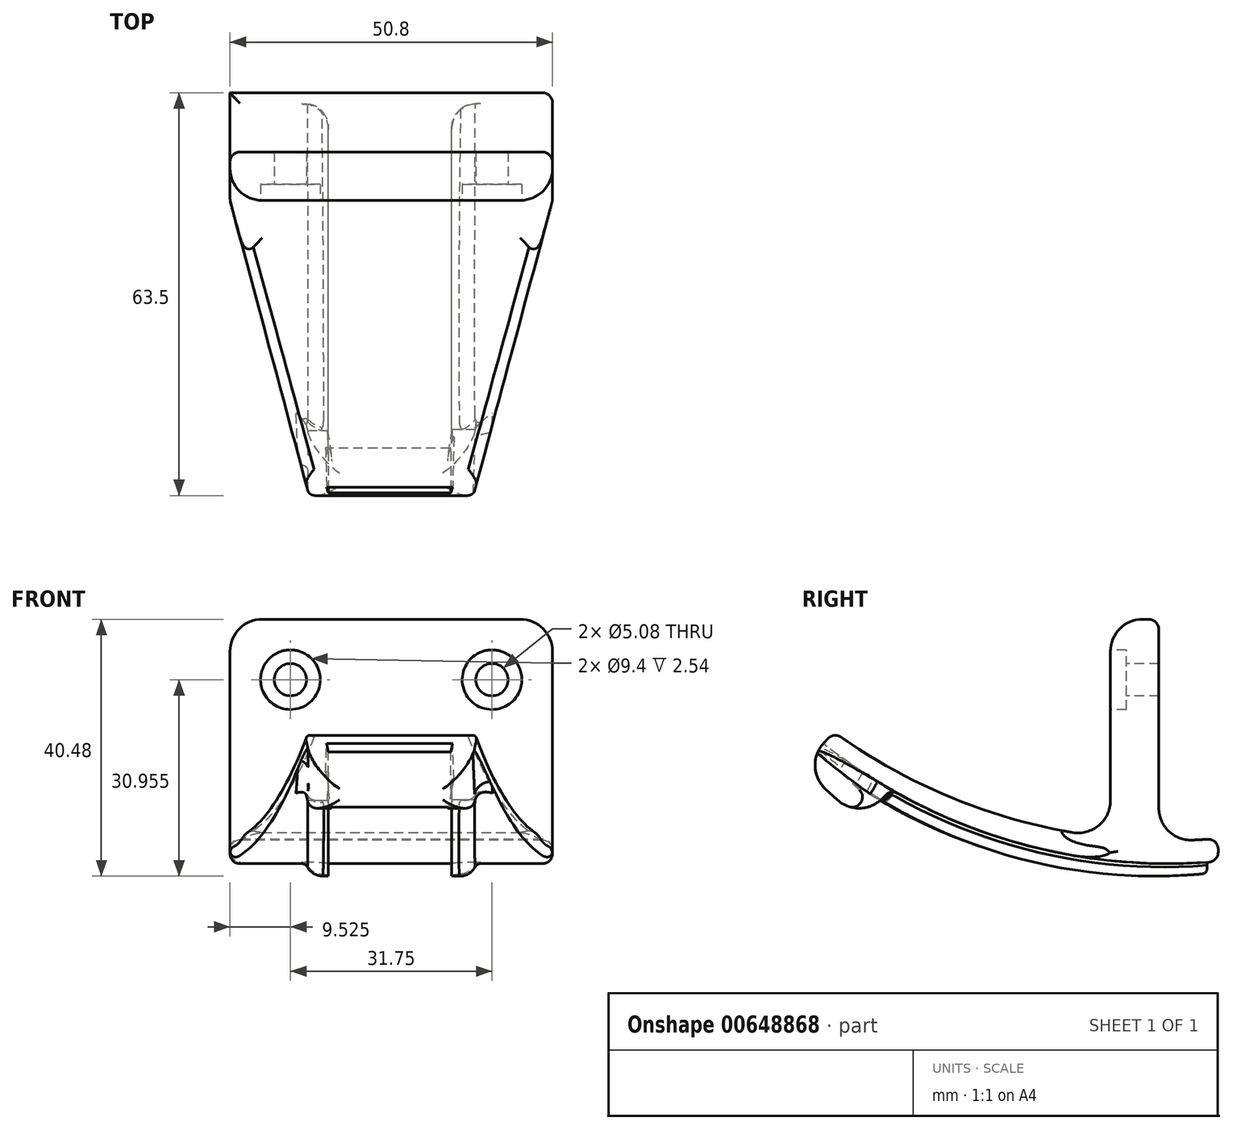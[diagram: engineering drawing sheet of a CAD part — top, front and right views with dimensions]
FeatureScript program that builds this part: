
annotation { "Feature Type Name" : "Feature", "Feature Type Description" : "" }
export const myFeature = defineFeature(function(context is Context, id is Id, definition is map)
    precondition{}
    {
        {
            var Q0;
            Q0=qCreatedBy(makeId("Front.planeOp"),FACE);
            var sketch = newSketch(context, id + "F0", { "sketchPlane" : qUnion([Q0])});
            skLineSegment(sketch, "E0.bottom", {"start": v(25.4, -17.78) * mm, "end": v(-25.4, -17.78) * mm});
            skLineSegment(sketch, "E0.top", {"start": v(25.4, 17.78) * mm, "end": v(-25.4, 17.78) * mm});
            skLineSegment(sketch, "E0.left", {"start": v(25.4, -17.78) * mm, "end": v(25.4, 17.78) * mm});
            skLineSegment(sketch, "E0.right", {"start": v(-25.4, -17.78) * mm, "end": v(-25.4, 17.78) * mm});
            skPoint(sketch, "E0.middle", {"position": v(0, 0) * mm});
            skPoint(sketch, "E1", {"position": v(-15.88, 8.26) * mm});
            skPoint(sketch, "E2", {"position": v(15.87, 8.26) * mm});
            skSolve(sketch);
        }
        {
            var Q0;
            Q0=makeQuery(id+"F0.imprint","IMPRINT",FACE,{"disambiguationData":[TD([[makeQuery(id+"F0.imprint","IMPRINT",EDGE,{"derivedFrom":sQuery(id+"F0.wireOp",EDGE,"E0.bottom")}),-1.0]])]});
            extrude(context, id + "F1", {"entities" : qUnion([Q0]), "oppositeDirection" : true, "depth" : 7.62 * mm, "offsetDistance" : 25.4 * mm});
        }
        {
            var Q0;
            Q0=qCreatedBy(makeId("Front.planeOp"),FACE);
            var sketch = newSketch(context, id + "F2", { "sketchPlane" : qUnion([Q0])});
            skPoint(sketch, "E3", {"position": v(-15.88, 8.26) * mm});
            skPoint(sketch, "E4", {"position": v(15.87, 8.26) * mm});
            skSolve(sketch);
        }
        {
            var Q0;
            Q0=sQuery(id+"F2.wireOp",VERTEX,"E3");
            var Q1;
            Q1=sQuery(id+"F2.wireOp",VERTEX,"E4");
            var Q2;
            Q2=makeQuery(id+"F1.opExtrude","SWEPT_BODY",BODY,{"disambiguationData":[OSD([sQuery(id+"F0.wireOp",EDGE,"E0.bottom"),sQuery(id+"F0.wireOp",EDGE,"E0.top"),sQuery(id+"F0.wireOp",EDGE,"E0.left"),sQuery(id+"F0.wireOp",EDGE,"E0.right")])]});
            hole(context, id + "F3", {"style" : HoleStyle.C_BORE, "endStyle" : HoleEndStyle.BLIND, "holeDiameter" : 5.08 * mm, "cBoreDiameter" : 9.4 * mm, "cBoreDepth" : 2.54 * mm, "majorDiameter" : 6.35 * mm, "holeDepth" : 7.62 * mm, "isTappedThrough" : true, "tappedDepth" : 12.7 * mm, "tapClearance" : 3, "locations" : qUnion([Q0, Q1]), "scope" : qUnion([Q2])});
        }
        {
            var Q0;
            Q0=qCreatedBy(makeId("Right.planeOp"),FACE);
            cPlane(context, id + "F4", {"entities" : qUnion([Q0]), "cplaneType" : CPlaneType.OFFSET, "offset" : 25.4 * mm, "oppositeDirection" : true, "width" : 152.4 * mm, "height" : 152.4 * mm});
        }
        {
            var Q0;
            Q0=qCreatedBy(id+"F4.planeOp",FACE);
            var sketch = newSketch(context, id + "F5", { "sketchPlane" : qUnion([Q0])});
            skArc(sketch, "E5", {"start": v(-43.55, 0) * mm, "mid": v(-14.8, -13.85) * mm, "end": v(16.98, -16.76) * mm});
            skArc(sketch, "E6", {"start": v(-45.22, -1.81) * mm, "mid": v(-15.9, -17.1) * mm, "end": v(16.98, -20.38) * mm});
            skLineSegment(sketch, "E7", {"start": v(-45.22, -1.81) * mm, "end": v(-43.55, 0) * mm});
            skLineSegment(sketch, "E8", {"start": v(16.98, -20.38) * mm, "end": v(16.98, -16.76) * mm});
            skSolve(sketch);
        }
        {
            var Q0;
            Q0=makeQuery(id+"F5.imprint","IMPRINT",FACE,{"disambiguationData":[TD([[makeQuery(id+"F5.imprint","IMPRINT",EDGE,{"derivedFrom":sQuery(id+"F5.wireOp",EDGE,"E5")}),-1.0]])]});
            extrude(context, id + "F6", {"entities" : qUnion([Q0]), "operationType" : NewBodyOperationType.ADD, "depth" : 50.8 * mm, "offsetDistance" : 25.4 * mm});
        }
        {
            var Q0;
            Q0=qCreatedBy(makeId("Right.planeOp"),FACE);
            var Q1;
            Q1=sQuery(id+"F0.wireOp",EDGE,"E0.left");
            cPlane(context, id + "F7", {"entities" : qUnion([Q0, Q1]), "cplaneType" : CPlaneType.LINE_ANGLE, "offset" : 25.4 * mm, "angle" : 15 * degree, "oppositeDirection" : true, "width" : 152.4 * mm, "height" : 152.4 * mm});
        }
        {
            var Q0;
            Q0=qCreatedBy(makeId("Right.planeOp"),FACE);
            var Q1;
            Q1=sQuery(id+"F0.wireOp",EDGE,"E0.right");
            cPlane(context, id + "F8", {"entities" : qUnion([Q0, Q1]), "cplaneType" : CPlaneType.LINE_ANGLE, "offset" : 25.4 * mm, "angle" : 15 * degree, "width" : 152.4 * mm, "height" : 152.4 * mm});
        }
        {
            var Q0;
            Q0=qCreatedBy(id+"F7.planeOp",FACE);
            var sketch = newSketch(context, id + "F9", { "sketchPlane" : qUnion([Q0])});
            skLineSegment(sketch, "E9.bottom", {"start": v(-11.2, 0) * mm, "end": v(43.96, 0) * mm});
            skLineSegment(sketch, "E9.top", {"start": v(-11.2, -22.32) * mm, "end": v(43.96, -22.32) * mm});
            skLineSegment(sketch, "E9.left", {"start": v(-11.2, 0) * mm, "end": v(-11.2, -22.32) * mm});
            skLineSegment(sketch, "E9.right", {"start": v(43.96, 0) * mm, "end": v(43.96, -22.32) * mm});
            skSolve(sketch);
        }
        {
            var Q0;
            Q0=makeQuery(id+"F9.imprint","IMPRINT",FACE,{"disambiguationData":[TD([[makeQuery(id+"F9.imprint","IMPRINT",EDGE,{"derivedFrom":sQuery(id+"F9.wireOp",EDGE,"E9.bottom")}),-1.0]])]});
            extrude(context, id + "F10", {"entities" : qUnion([Q0]), "operationType" : NewBodyOperationType.REMOVE, "oppositeDirection" : true, "depth" : 25.4 * mm, "offsetDistance" : 25.4 * mm});
        }
        {
            var Q0;
            Q0=qCreatedBy(id+"F8.planeOp",FACE);
            var sketch = newSketch(context, id + "F11", { "sketchPlane" : qUnion([Q0])});
            skLineSegment(sketch, "E10.bottom", {"start": v(-10.77, 0.83) * mm, "end": v(45.1, 0.83) * mm});
            skLineSegment(sketch, "E10.top", {"start": v(-10.77, -22.12) * mm, "end": v(45.1, -22.12) * mm});
            skLineSegment(sketch, "E10.left", {"start": v(-10.77, 0.83) * mm, "end": v(-10.77, -22.12) * mm});
            skLineSegment(sketch, "E10.right", {"start": v(45.1, 0.83) * mm, "end": v(45.1, -22.12) * mm});
            skSolve(sketch);
        }
        {
            var Q0;
            Q0=makeQuery(id+"F11.imprint","IMPRINT",FACE,{"disambiguationData":[TD([[makeQuery(id+"F11.imprint","IMPRINT",EDGE,{"derivedFrom":sQuery(id+"F11.wireOp",EDGE,"E10.bottom")}),-1.0]])]});
            extrude(context, id + "F12", {"entities" : qUnion([Q0]), "operationType" : NewBodyOperationType.REMOVE, "depth" : 25.4 * mm, "offsetDistance" : 25.4 * mm});
        }
        {
            var Q0;
            Q0=makeQuery(id+"F6.opExtrude","SWEPT_FACE",FACE,{"disambiguationData":[OSD([sQuery(id+"F5.wireOp",EDGE,"E7")])]});
            var sketch = newSketch(context, id + "F13", { "sketchPlane" : qUnion([Q0])});
            skLineSegment(sketch, "E11", {"start": v(13.73, -29.43) * mm, "end": v(12.37, -36.93) * mm});
            skLineSegment(sketch, "E12", {"start": v(-13.73, -29.43) * mm, "end": v(-12.37, -36.93) * mm});
            skLineSegment(sketch, "E13", {"start": v(-12.37, -36.93) * mm, "end": v(12.37, -36.93) * mm});
            skLineSegment(sketch, "E14", {"start": v(13.73, -29.43) * mm, "end": v(10.12, -29.43) * mm});
            skLineSegment(sketch, "E15", {"start": v(10.12, -29.43) * mm, "end": v(9.4, -33.43) * mm});
            skLineSegment(sketch, "E16", {"start": v(-10.63, -29.43) * mm, "end": v(-9.9, -33.43) * mm});
            skLineSegment(sketch, "E17", {"start": v(-9.9, -33.43) * mm, "end": v(9.4, -33.43) * mm});
            skLineSegment(sketch, "E18.trimOffspring", {"start": v(-10.63, -29.43) * mm, "end": v(-13.73, -29.43) * mm});
            skSolve(sketch);
        }
        {
            var Q0;
            {var subQ4=sQuery(id+"F13.wireOp",EDGE,"E13");Q0=makeQuery(id+"F13.imprint","IMPRINT",FACE,{"disambiguationData":[TD([[makeQuery(id+"F13.imprint","IMPRINT",EDGE,{"derivedFrom":subQ4}),1.0]])]});}
            var Q1;
            {var subQ0=sQuery(id+"F13.wireOp",EDGE,"E14");Q1=makeQuery(id+"F13.imprint","IMPRINT",FACE,{"disambiguationData":[TD([[makeQuery(id+"F13.imprint","IMPRINT",EDGE,{"derivedFrom":subQ0}),1.0]])]});}
            var Q2;
            {var subQ0=sQuery(id+"F13.wireOp",EDGE,"E18.trimOffspring");Q2=makeQuery(id+"F13.imprint","IMPRINT",FACE,{"disambiguationData":[TD([[makeQuery(id+"F13.imprint","IMPRINT",EDGE,{"derivedFrom":subQ0}),1.0]])]});}
            extrude(context, id + "F14", {"entities" : qUnion([Q0, Q1, Q2]), "operationType" : NewBodyOperationType.ADD, "oppositeDirection" : true, "depth" : 12.7 * mm, "offsetDistance" : 25.4 * mm});
        }
        {
            var Q0;
            Q0=makeQuery(id+"F14.opExtrude","CAP_EDGE",EDGE,{"disambiguationData":[OSD([sQuery(id+"F13.wireOp",EDGE,"E13")])],"isStart":false});
            var Q1;
            Q1=makeQuery(id+"F14.opExtrude","CAP_EDGE",EDGE,{"disambiguationData":[OSD([sQuery(id+"F13.wireOp",EDGE,"E13")])],"isStart":true});
            var Q2;
            Q2=makeQuery(id+"F14.opExtrude","SWEPT_EDGE",EDGE,{"disambiguationData":[OSD([sQuery(id+"F13.wireOp",EDGE,"E12"),sQuery(id+"F13.wireOp",EDGE,"E13")])]});
            var Q3;
            Q3=makeQuery(id+"F14.opExtrude","SWEPT_EDGE",EDGE,{"disambiguationData":[OSD([sQuery(id+"F13.wireOp",EDGE,"E11"),sQuery(id+"F13.wireOp",EDGE,"E13")])]});
            var Q4;
            Q4=makeQuery(id+"F6.boolean.opBoolean","INTERSECT",EDGE,{"derivedFrom":[makeQuery(id+"F1.opExtrude","CAP_FACE",FACE,{"disambiguationData":[OSD([sQuery(id+"F0.wireOp",EDGE,"E0.bottom"),sQuery(id+"F0.wireOp",EDGE,"E0.top"),sQuery(id+"F0.wireOp",EDGE,"E0.left"),sQuery(id+"F0.wireOp",EDGE,"E0.right")])],"isStart":false}),makeQuery(id+"F6.opExtrude","SWEPT_FACE",FACE,{"disambiguationData":[OSD([sQuery(id+"F5.wireOp",EDGE,"E5")])]})]});
            var Q5;
            Q5=makeQuery(id+"F6.boolean.opBoolean","INTERSECT",EDGE,{"derivedFrom":[makeQuery(id+"F1.opExtrude","CAP_FACE",FACE,{"disambiguationData":[OSD([sQuery(id+"F0.wireOp",EDGE,"E0.bottom"),sQuery(id+"F0.wireOp",EDGE,"E0.top"),sQuery(id+"F0.wireOp",EDGE,"E0.left"),sQuery(id+"F0.wireOp",EDGE,"E0.right")])],"isStart":true}),makeQuery(id+"F6.opExtrude","SWEPT_FACE",FACE,{"disambiguationData":[OSD([sQuery(id+"F5.wireOp",EDGE,"E5")])]})]});
            var Q6;
            Q6=makeQuery(id+"F1.opExtrude","CAP_EDGE",EDGE,{"disambiguationData":[OSD([sQuery(id+"F0.wireOp",EDGE,"E0.top")])],"isStart":true});
            fillet(context, id + "F15", {"entities" : qUnion([Q0, Q1, Q2, Q3, Q4, Q5, Q6]), "radius" : 5.08 * mm, "tangentPropagation" : true, "allowEdgeOverflow" : false});
        }
        {
            var Q0;
            Q0=makeQuery(id+"F1.opExtrude","CAP_EDGE",EDGE,{"disambiguationData":[OSD([sQuery(id+"F0.wireOp",EDGE,"E0.left")])],"isStart":true});
            var Q1;
            Q1=makeQuery(id+"F1.opExtrude","CAP_EDGE",EDGE,{"disambiguationData":[OSD([sQuery(id+"F0.wireOp",EDGE,"E0.right")])],"isStart":true});
            fillet(context, id + "F16", {"entities" : qUnion([Q0, Q1]), "radius" : 5.08 * mm, "tangentPropagation" : true, "allowEdgeOverflow" : false});
        }
        {
            var Q0;
            Q0=makeQuery(id+"F14.boolean.opBoolean","INTERSECT",EDGE,{"derivedFrom":[makeQuery(id+"F6.opExtrude","SWEPT_FACE",FACE,{"disambiguationData":[OSD([sQuery(id+"F5.wireOp",EDGE,"E6")])]}),makeQuery(id+"F14.opExtrude","SWEPT_FACE",FACE,{"disambiguationData":[OSD([sQuery(id+"F13.wireOp",EDGE,"E12")])]})]});
            var Q1;
            Q1=makeQuery(id+"F14.boolean.opBoolean","INTERSECT",EDGE,{"disambiguationData":[OD(1.0)],"derivedFrom":[makeQuery(id+"F6.opExtrude","SWEPT_FACE",FACE,{"disambiguationData":[OSD([sQuery(id+"F5.wireOp",EDGE,"E6")])]}),makeQuery(id+"F14.opExtrude","CAP_FACE",FACE,{"disambiguationData":[OSD([sQuery(id+"F13.wireOp",EDGE,"E11"),sQuery(id+"F13.wireOp",EDGE,"E12"),sQuery(id+"F13.wireOp",EDGE,"E13"),sQuery(id+"F13.wireOp",EDGE,"E14"),sQuery(id+"F13.wireOp",EDGE,"E15"),sQuery(id+"F13.wireOp",EDGE,"E16"),sQuery(id+"F13.wireOp",EDGE,"E17"),sQuery(id+"F13.wireOp",EDGE,"E18.trimOffspring")])],"isStart":false})]});
            var Q2;
            Q2=makeQuery(id+"F14.boolean.opBoolean","INTERSECT",EDGE,{"disambiguationData":[OD(0.0)],"derivedFrom":[makeQuery(id+"F6.opExtrude","SWEPT_FACE",FACE,{"disambiguationData":[OSD([sQuery(id+"F5.wireOp",EDGE,"E6")])]}),makeQuery(id+"F14.opExtrude","CAP_FACE",FACE,{"disambiguationData":[OSD([sQuery(id+"F13.wireOp",EDGE,"E11"),sQuery(id+"F13.wireOp",EDGE,"E12"),sQuery(id+"F13.wireOp",EDGE,"E13"),sQuery(id+"F13.wireOp",EDGE,"E14"),sQuery(id+"F13.wireOp",EDGE,"E15"),sQuery(id+"F13.wireOp",EDGE,"E16"),sQuery(id+"F13.wireOp",EDGE,"E17"),sQuery(id+"F13.wireOp",EDGE,"E18.trimOffspring")])],"isStart":false})]});
            var Q3;
            Q3=makeQuery(id+"F15.opFillet","BLEND_EDGE",EDGE,{"blendedFrom":[makeQuery(id+"F14.opExtrude","CAP_EDGE",EDGE,{"disambiguationData":[OSD([sQuery(id+"F13.wireOp",EDGE,"E13")])],"isStart":false}),makeQuery(id+"F14.opExtrude","SWEPT_FACE",FACE,{"disambiguationData":[OSD([sQuery(id+"F13.wireOp",EDGE,"E17")])]})],"blendedInto":[makeQuery(id+"F14.opExtrude","SWEPT_FACE",FACE,{"disambiguationData":[OSD([sQuery(id+"F13.wireOp",EDGE,"E17")])]})]});
            var Q4;
            {var subQ3=sQuery(id+"F5.wireOp",EDGE,"E7");var subQ5=sQuery(id+"F5.wireOp",EDGE,"E5");Q4=makeQuery(id+"F10.boolean.opBoolean","INTERSECT",EDGE,{"derivedFrom":[makeQuery(id+"F6.boolean.opBoolean","SPLIT",FACE,{"disambiguationData":[TD([makeQuery(id+"F6.opExtrude","SWEPT_FACE",FACE,{"disambiguationData":[OSD([subQ3])]})])],"derivedFrom":makeQuery(id+"F6.opExtrude","SWEPT_FACE",FACE,{"disambiguationData":[OSD([subQ5])]})}),makeQuery(id+"F10.opExtrude","CAP_FACE",FACE,{"disambiguationData":[OSD([sQuery(id+"F9.wireOp",EDGE,"E9.bottom"),sQuery(id+"F9.wireOp",EDGE,"E9.top"),sQuery(id+"F9.wireOp",EDGE,"E9.left"),sQuery(id+"F9.wireOp",EDGE,"E9.right")])],"isStart":true})]});}
            var Q5;
            Q5=makeQuery(id+"F6.opExtrude","SWEPT_EDGE",EDGE,{"disambiguationData":[OSD([sQuery(id+"F5.wireOp",EDGE,"E5"),sQuery(id+"F5.wireOp",EDGE,"E7")])]});
            var Q6;
            {var subQ3=sQuery(id+"F5.wireOp",EDGE,"E7");var subQ5=sQuery(id+"F5.wireOp",EDGE,"E5");Q6=makeQuery(id+"F12.boolean.opBoolean","INTERSECT",EDGE,{"derivedFrom":[makeQuery(id+"F6.boolean.opBoolean","SPLIT",FACE,{"disambiguationData":[TD([makeQuery(id+"F6.opExtrude","SWEPT_FACE",FACE,{"disambiguationData":[OSD([subQ3])]})])],"derivedFrom":makeQuery(id+"F6.opExtrude","SWEPT_FACE",FACE,{"disambiguationData":[OSD([subQ5])]})}),makeQuery(id+"F12.opExtrude","CAP_FACE",FACE,{"disambiguationData":[OSD([sQuery(id+"F11.wireOp",EDGE,"E10.bottom"),sQuery(id+"F11.wireOp",EDGE,"E10.top"),sQuery(id+"F11.wireOp",EDGE,"E10.left"),sQuery(id+"F11.wireOp",EDGE,"E10.right")])],"isStart":true})]});}
            var Q7;
            Q7=makeQuery(id+"F6.opExtrude","CAP_EDGE",EDGE,{"disambiguationData":[OSD([sQuery(id+"F5.wireOp",EDGE,"E6")])],"isStart":true});
            var Q8;
            Q8=makeQuery(id+"F6.opExtrude","SWEPT_EDGE",EDGE,{"disambiguationData":[OSD([sQuery(id+"F5.wireOp",EDGE,"E6"),sQuery(id+"F5.wireOp",EDGE,"E8")])]});
            var Q9;
            {var subQ0=sQuery(id+"F5.wireOp",EDGE,"E8");var subQ1=sQuery(id+"F5.wireOp",EDGE,"E5");Q9=makeQuery(id+"F6.boolean.opBoolean","SPLIT",EDGE,{"disambiguationData":[TD([makeQuery(id+"F6.opExtrude","SWEPT_FACE",FACE,{"disambiguationData":[OSD([subQ0])]})])],"derivedFrom":makeQuery(id+"F6.opExtrude","CAP_EDGE",EDGE,{"disambiguationData":[OSD([subQ1])],"isStart":true})});}
            var Q10;
            Q10=makeQuery(id+"F6.opExtrude","SWEPT_EDGE",EDGE,{"disambiguationData":[OSD([sQuery(id+"F5.wireOp",EDGE,"E5"),sQuery(id+"F5.wireOp",EDGE,"E8")])]});
            var Q11;
            Q11=makeQuery(id+"F6.opExtrude","CAP_EDGE",EDGE,{"disambiguationData":[OSD([sQuery(id+"F5.wireOp",EDGE,"E8")])],"isStart":false});
            var Q12;
            Q12=makeQuery(id+"F6.opExtrude","CAP_EDGE",EDGE,{"disambiguationData":[OSD([sQuery(id+"F5.wireOp",EDGE,"E6")])],"isStart":false});
            fillet(context, id + "F17", {"entities" : qUnion([Q0, Q1, Q2, Q3, Q4, Q5, Q6, Q7, Q8, Q9, Q10, Q11, Q12]), "radius" : 1.59 * mm, "tangentPropagation" : true, "allowEdgeOverflow" : false});
        }
        {
            var Q0;
            Q0=makeQuery(id+"F14.boolean.opBoolean","INTERSECT",EDGE,{"derivedFrom":[makeQuery(id+"F6.opExtrude","SWEPT_FACE",FACE,{"disambiguationData":[OSD([sQuery(id+"F5.wireOp",EDGE,"E6")])]}),makeQuery(id+"F14.opExtrude","SWEPT_FACE",FACE,{"disambiguationData":[OSD([sQuery(id+"F13.wireOp",EDGE,"E11")])]})]});
            fillet(context, id + "F18", {"entities" : qUnion([Q0]), "radius" : 2.76 * mm, "tangentPropagation" : true, "allowEdgeOverflow" : false});
        }
        {
            var Q0;
            Q0=qCreatedBy(makeId("Right.planeOp"),FACE);
            cPlane(context, id + "F19", {"entities" : qUnion([Q0]), "cplaneType" : CPlaneType.OFFSET, "offset" : 9.9 * mm, "width" : 152.4 * mm, "height" : 152.4 * mm});
        }
        {
            var Q0;
            Q0=qCreatedBy(makeId("Right.planeOp"),FACE);
            cPlane(context, id + "F20", {"entities" : qUnion([Q0]), "cplaneType" : CPlaneType.OFFSET, "offset" : 9.9 * mm, "oppositeDirection" : true, "width" : 152.4 * mm, "height" : 152.4 * mm});
        }
        {
            var Q0;
            Q0=qCreatedBy(id+"F19.planeOp",FACE);
            var sketch = newSketch(context, id + "F21", { "sketchPlane" : qUnion([Q0])});
            skArc(sketch, "E19", {"start": v(-37.12, -7.15) * mm, "mid": v(-11.97, -17.63) * mm, "end": v(15.19, -19.92) * mm});
            skArc(sketch, "E20", {"start": v(-38.33, -9.3) * mm, "mid": v(-12.6, -20.38) * mm, "end": v(15.35, -22.26) * mm});
            skLineSegment(sketch, "E21", {"start": v(15.35, -22.26) * mm, "end": v(15.19, -19.92) * mm});
            skLineSegment(sketch, "E22", {"start": v(-38.33, -9.3) * mm, "end": v(-37.12, -7.15) * mm});
            skSolve(sketch);
        }
        {
            var Q0;
            Q0=makeQuery(id+"F21.imprint","IMPRINT",FACE,{"disambiguationData":[TD([[makeQuery(id+"F21.imprint","IMPRINT",EDGE,{"derivedFrom":sQuery(id+"F21.wireOp",EDGE,"E19")}),-1.0]])]});
            extrude(context, id + "F22", {"entities" : qUnion([Q0]), "operationType" : NewBodyOperationType.ADD, "depth" : 3.17 * mm, "offsetDistance" : 25.4 * mm, "hasSecondDirection" : true, "secondDirectionOppositeDirection" : true, "secondDirectionDepth" : 0.38 * mm});
        }
        {
            var Q0;
            Q0=qCreatedBy(id+"F20.planeOp",FACE);
            var sketch = newSketch(context, id + "F23", { "sketchPlane" : qUnion([Q0])});
            skArc(sketch, "E23", {"start": v(-38.76, -5.91) * mm, "mid": v(-12.95, -16.98) * mm, "end": v(15.02, -19.36) * mm});
            skArc(sketch, "E24", {"start": v(-40.16, -8.33) * mm, "mid": v(-13.57, -20.1) * mm, "end": v(15.43, -22.28) * mm});
            skLineSegment(sketch, "E25", {"start": v(15.43, -22.28) * mm, "end": v(15.02, -19.36) * mm});
            skLineSegment(sketch, "E26", {"start": v(-40.16, -8.33) * mm, "end": v(-38.76, -5.91) * mm});
            skSolve(sketch);
        }
        {
            var Q0;
            Q0=makeQuery(id+"F23.imprint","IMPRINT",FACE,{"disambiguationData":[TD([[makeQuery(id+"F23.imprint","IMPRINT",EDGE,{"derivedFrom":sQuery(id+"F23.wireOp",EDGE,"E23")}),-1.0]])]});
            extrude(context, id + "F24", {"entities" : qUnion([Q0]), "operationType" : NewBodyOperationType.ADD, "oppositeDirection" : true, "depth" : 3.17 * mm, "offsetDistance" : 25.4 * mm});
        }
        {
            var Q0;
            Q0=makeQuery(id+"F22.boolean.opBoolean","INTERSECT",EDGE,{"derivedFrom":[makeQuery(id+"F6.opExtrude","SWEPT_FACE",FACE,{"disambiguationData":[OSD([sQuery(id+"F5.wireOp",EDGE,"E6")])]}),makeQuery(id+"F22.opExtrude","CAP_FACE",FACE,{"disambiguationData":[OSD([sQuery(id+"F21.wireOp",EDGE,"E19"),sQuery(id+"F21.wireOp",EDGE,"E20"),sQuery(id+"F21.wireOp",EDGE,"E21"),sQuery(id+"F21.wireOp",EDGE,"E22")])],"isStart":false})]});
            var Q1;
            Q1=makeQuery(id+"F24.boolean.opBoolean","INTERSECT",EDGE,{"derivedFrom":[makeQuery(id+"F6.opExtrude","SWEPT_FACE",FACE,{"disambiguationData":[OSD([sQuery(id+"F5.wireOp",EDGE,"E6")])]}),makeQuery(id+"F24.opExtrude","CAP_FACE",FACE,{"disambiguationData":[OSD([sQuery(id+"F23.wireOp",EDGE,"E23"),sQuery(id+"F23.wireOp",EDGE,"E24"),sQuery(id+"F23.wireOp",EDGE,"E25"),sQuery(id+"F23.wireOp",EDGE,"E26")])],"isStart":false})]});
            fillet(context, id + "F25", {"entities" : qUnion([Q0, Q1]), "radius" : 1.02 * mm, "tangentPropagation" : true, "allowEdgeOverflow" : false});
        }
        {
            var Q0;
            Q0=makeQuery(id+"F22.opExtrude","CAP_EDGE",EDGE,{"disambiguationData":[OSD([sQuery(id+"F21.wireOp",EDGE,"E20")])],"isStart":false});
            var Q1;
            {var subQ1=sQuery(id+"F23.wireOp",EDGE,"E25");var subQ2=sQuery(id+"F23.wireOp",EDGE,"E24");Q1=makeQuery(id+"F24.boolean.opBoolean","SPLIT",EDGE,{"disambiguationData":[TD([makeQuery(id+"F24.opExtrude","SWEPT_FACE",FACE,{"disambiguationData":[OSD([subQ1])]})])],"derivedFrom":makeQuery(id+"F24.opExtrude","CAP_EDGE",EDGE,{"disambiguationData":[OSD([subQ2])],"isStart":false})});}
            fillet(context, id + "F26", {"entities" : qUnion([Q0, Q1]), "radius" : 2.7 * mm, "tangentPropagation" : true, "allowEdgeOverflow" : false});
        }
        {
            var Q0;
            Q0=makeQuery(id+"F22.opExtrude","CAP_EDGE",EDGE,{"disambiguationData":[OSD([sQuery(id+"F21.wireOp",EDGE,"E21")])],"isStart":true});
            var Q1;
            Q1=makeQuery(id+"F24.opExtrude","CAP_EDGE",EDGE,{"disambiguationData":[OSD([sQuery(id+"F23.wireOp",EDGE,"E25")])],"isStart":true});
            fillet(context, id + "F27", {"entities" : qUnion([Q0, Q1]), "radius" : 4 * mm, "tangentPropagation" : true, "allowEdgeOverflow" : false});
        }
    });
